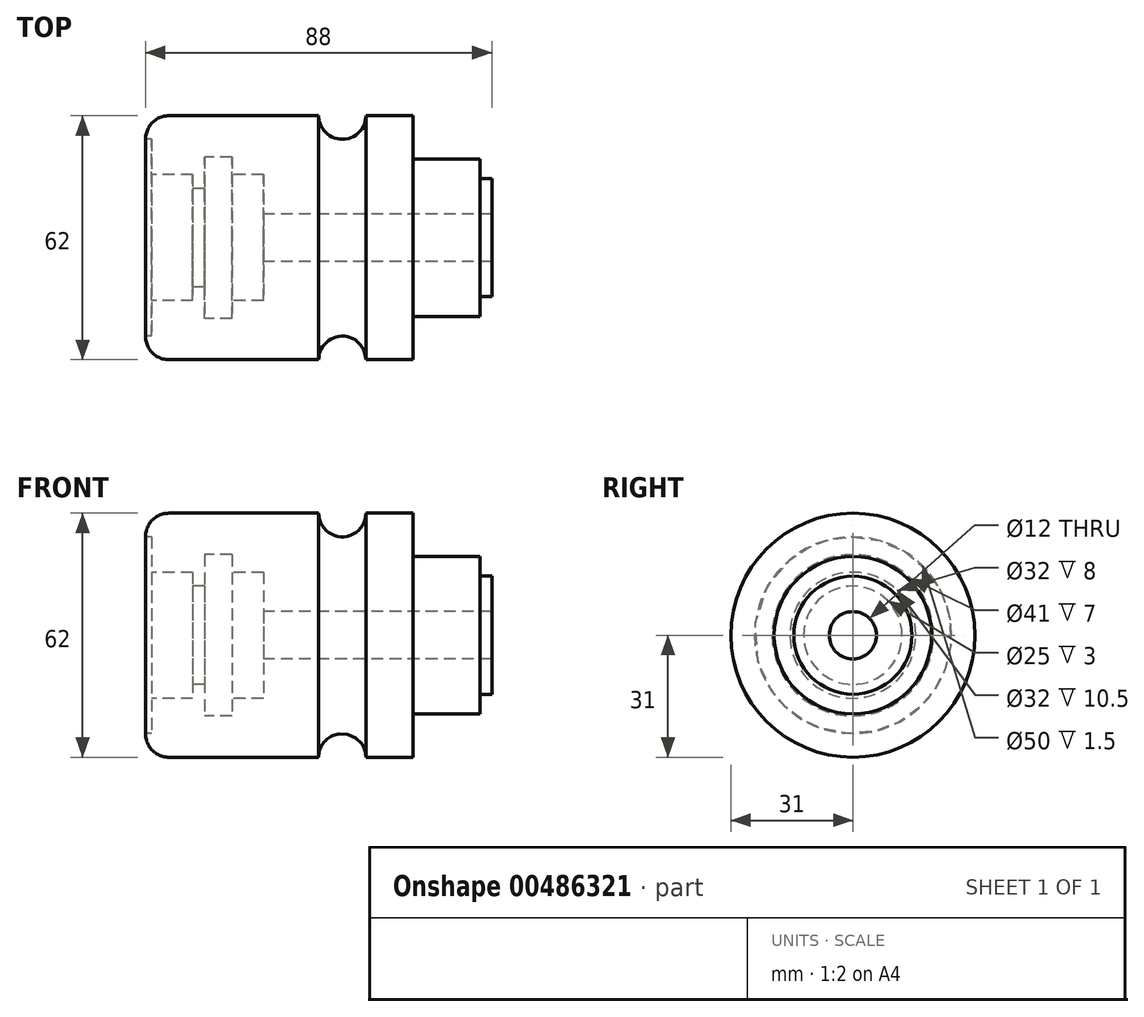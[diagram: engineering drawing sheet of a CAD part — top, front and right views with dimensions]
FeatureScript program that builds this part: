
annotation { "Feature Type Name" : "Feature", "Feature Type Description" : "" }
export const myFeature = defineFeature(function(context is Context, id is Id, definition is map)
    precondition{}
    {
        {
            var Q0;
            Q0=qCreatedBy(makeId("Front.planeOp"),FACE);
            var sketch = newSketch(context, id + "F0", { "sketchPlane" : qUnion([Q0])});
            skLineSegment(sketch, "E0", {"start": v(0, 0) * mm, "end": v(114.82, 0) * mm});
            skLineSegment(sketch, "E1", {"start": v(0, 0) * mm, "end": v(0, 31) * mm});
            skLineSegment(sketch, "E2", {"start": v(0, 31) * mm, "end": v(44, 31) * mm});
            skLineSegment(sketch, "E3", {"start": v(68, 31) * mm, "end": v(68, 20) * mm});
            skLineSegment(sketch, "E4", {"start": v(68, 20) * mm, "end": v(85, 20) * mm});
            skLineSegment(sketch, "E5", {"start": v(85, 20) * mm, "end": v(85, 15) * mm});
            skLineSegment(sketch, "E6", {"start": v(85, 15) * mm, "end": v(88, 15) * mm});
            skLineSegment(sketch, "E7", {"start": v(88, 15) * mm, "end": v(88, 0) * mm});
            skArc(sketch, "E8", {"start": v(44, 31) * mm, "mid": v(50, 25) * mm, "end": v(56, 31) * mm});
            skLineSegment(sketch, "E9.trimOffspring", {"start": v(56, 31) * mm, "end": v(68, 31) * mm});
            skSolve(sketch);
        }
        {
            var Q0;
            Q0 = qSketchRegion(id + "F0", true);
            var Q1;
            Q1=sQuery(id+"F0.wireOp",EDGE,"E0");
            revolve(context, id + "F1", {"entities" : qUnion([Q0]), "axis" : qUnion([Q1]), "revolveType" : RevolveType.FULL});
        }
        {
            var Q0;
            Q0=qCreatedBy(makeId("Front.planeOp"),FACE);
            var sketch = newSketch(context, id + "F2", { "sketchPlane" : qUnion([Q0])});
            skLineSegment(sketch, "E10", {"start": v(0, 0) * mm, "end": v(0, 25) * mm});
            skLineSegment(sketch, "E11", {"start": v(0, 25) * mm, "end": v(1.5, 25) * mm});
            skLineSegment(sketch, "E12", {"start": v(1.5, 25) * mm, "end": v(1.5, 16) * mm});
            skLineSegment(sketch, "E13", {"start": v(1.5, 16) * mm, "end": v(12, 16) * mm});
            skLineSegment(sketch, "E14", {"start": v(12, 16) * mm, "end": v(12, 12.5) * mm});
            skLineSegment(sketch, "E15", {"start": v(12, 12.5) * mm, "end": v(15, 12.5) * mm});
            skLineSegment(sketch, "E16", {"start": v(22, 16) * mm, "end": v(30, 16) * mm});
            skLineSegment(sketch, "E17", {"start": v(30, 16) * mm, "end": v(30, 6) * mm});
            skLineSegment(sketch, "E18", {"start": v(30, 6) * mm, "end": v(88, 6) * mm});
            skLineSegment(sketch, "E19", {"start": v(88, 6) * mm, "end": v(88, 0) * mm});
            skLineSegment(sketch, "E20", {"start": v(88, 0) * mm, "end": v(0, 0) * mm});
            skLineSegment(sketch, "E21", {"start": v(-2.6, 0) * mm, "end": v(-23.25, 0) * mm, "construction": true});
            skLineSegment(sketch, "E22", {"start": v(15, 20.5) * mm, "end": v(22, 20.5) * mm});
            skPoint(sketch, "E22.startSnap0", {"position": v(22, 20.5) * mm});
            skLineSegment(sketch, "E23", {"start": v(15, 20.5) * mm, "end": v(15, 12.5) * mm});
            skLineSegment(sketch, "E24", {"start": v(22, 20.5) * mm, "end": v(22, 16) * mm});
            skSolve(sketch);
        }
        {
            var Q0;
            Q0 = qSketchRegion(id + "F2", true);
            var Q1;
            Q1=sQuery(id+"F2.wireOp",EDGE,"E21");
            revolve(context, id + "F3", {"operationType" : NewBodyOperationType.REMOVE, "entities" : qUnion([Q0]), "axis" : qUnion([Q1]), "revolveType" : RevolveType.FULL, "oppositeDirection" : true});
        }
        {
            var Q0;
            Q0=makeQuery(id+"F1.opRevolve","SWEPT_EDGE",EDGE,{"disambiguationData":[OSD([sQuery(id+"F0.wireOp",EDGE,"E1"),sQuery(id+"F0.wireOp",EDGE,"E2")])]});
            fillet(context, id + "F4", {"entities" : qUnion([Q0]), "radius" : 6 * mm, "tangentPropagation" : true, "allowEdgeOverflow" : false});
        }
    });
